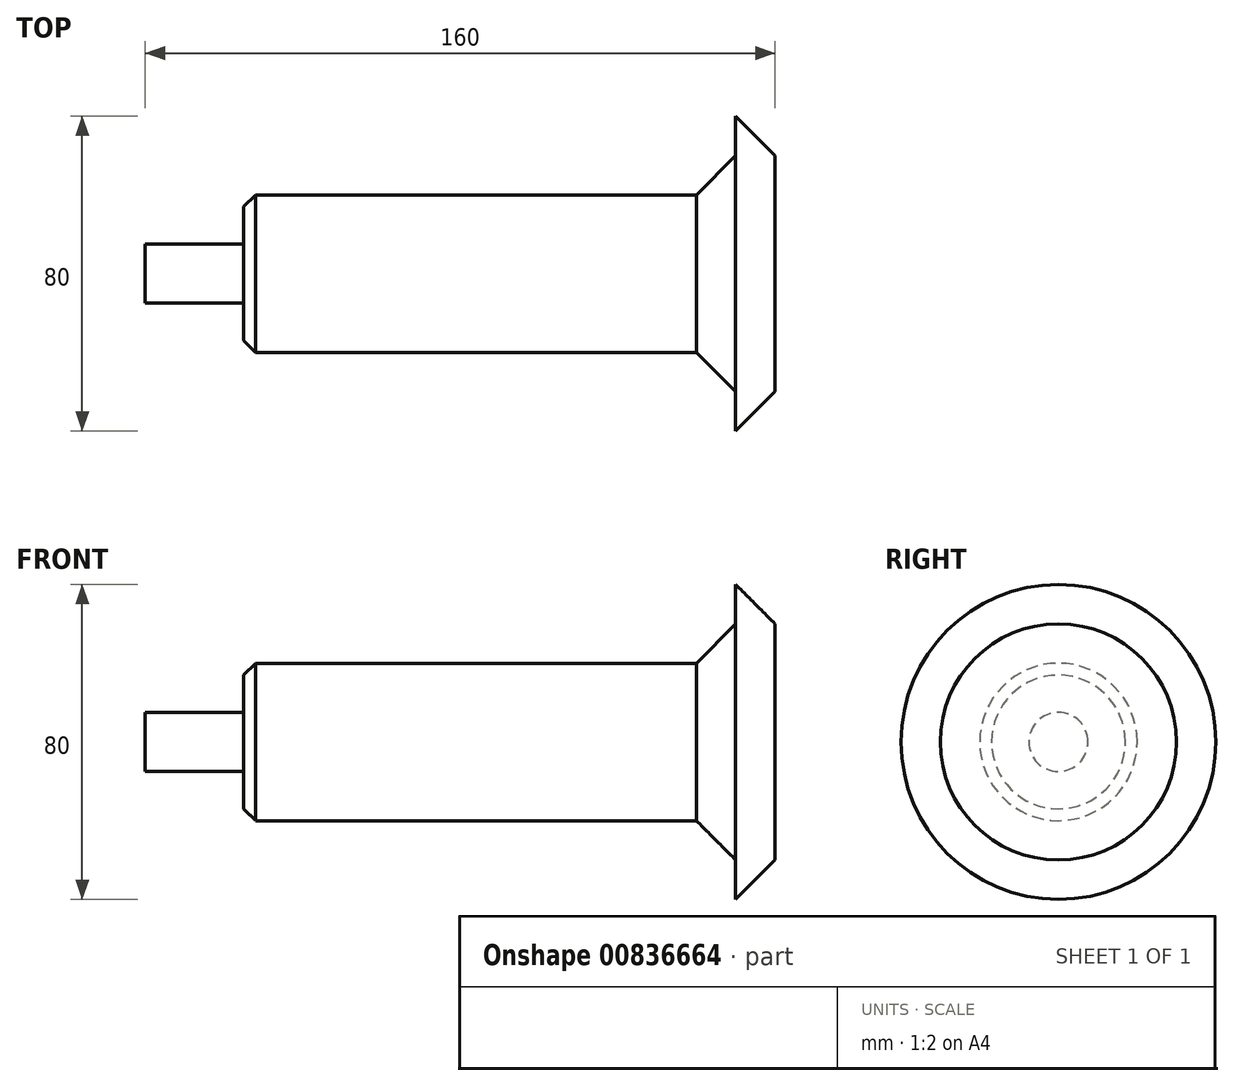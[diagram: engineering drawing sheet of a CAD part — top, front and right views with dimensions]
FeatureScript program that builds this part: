
annotation { "Feature Type Name" : "Feature", "Feature Type Description" : "" }
export const myFeature = defineFeature(function(context is Context, id is Id, definition is map)
    precondition{}
    {
        {
            var Q0;
            Q0=qCreatedBy(makeId("Top.planeOp"),FACE);
            var sketch = newSketch(context, id + "F0", { "sketchPlane" : qUnion([Q0])});
            skLineSegment(sketch, "E0", {"start": v(0, 0) * mm, "end": v(0, 7.5) * mm});
            skLineSegment(sketch, "E1", {"start": v(0, 7.5) * mm, "end": v(25, 7.5) * mm});
            skLineSegment(sketch, "E2", {"start": v(25, 7.5) * mm, "end": v(25, 20) * mm});
            skLineSegment(sketch, "E3", {"start": v(25, 20) * mm, "end": v(150, 20) * mm});
            skLineSegment(sketch, "E4", {"start": v(150, 40) * mm, "end": v(160, 40) * mm});
            skLineSegment(sketch, "E5", {"start": v(160, 40) * mm, "end": v(160, 0) * mm});
            skLineSegment(sketch, "E6", {"start": v(160, 0) * mm, "end": v(0, 0) * mm});
            skLineSegment(sketch, "E7", {"start": v(150, 20) * mm, "end": v(150, 40) * mm});
            skSolve(sketch);
        }
        {
            var Q0;
            Q0=makeQuery(id+"F0.imprint","IMPRINT",FACE,{"disambiguationData":[TD([[makeQuery(id+"F0.imprint","IMPRINT",EDGE,{"derivedFrom":sQuery(id+"F0.wireOp",EDGE,"E0")}),-1.0]])]});
            var Q1;
            Q1=sQuery(id+"F0.wireOp",EDGE,"E6");
            revolve(context, id + "F1", {"surfaceOperationType" : NewSurfaceOperationType.NEW, "entities" : qUnion([Q0]), "axis" : qUnion([Q1]), "revolveType" : RevolveType.FULL});
        }
        {
            var Q0;
            Q0=makeQuery(id+"F1.opRevolve","SWEPT_EDGE",EDGE,{"disambiguationData":[OSD([sQuery(id+"F0.wireOp",EDGE,"E2"),sQuery(id+"F0.wireOp",EDGE,"E3")])]});
            chamfer(context, id + "F2", {"entities" : qUnion([Q0]), "width" : 3 * mm, "tangentPropagation" : true});
        }
        {
            var Q0;
            Q0=makeQuery(id+"F1.opRevolve","SWEPT_EDGE",EDGE,{"disambiguationData":[OSD([sQuery(id+"F0.wireOp",EDGE,"E3"),sQuery(id+"F0.wireOp",EDGE,"E7")])]});
            var Q1;
            Q1=makeQuery(id+"F1.opRevolve","SWEPT_EDGE",EDGE,{"disambiguationData":[OSD([sQuery(id+"F0.wireOp",EDGE,"E4"),sQuery(id+"F0.wireOp",EDGE,"E5")])]});
            chamfer(context, id + "F3", {"entities" : qUnion([Q0, Q1]), "width" : 10 * mm, "tangentPropagation" : true});
        }
    });
